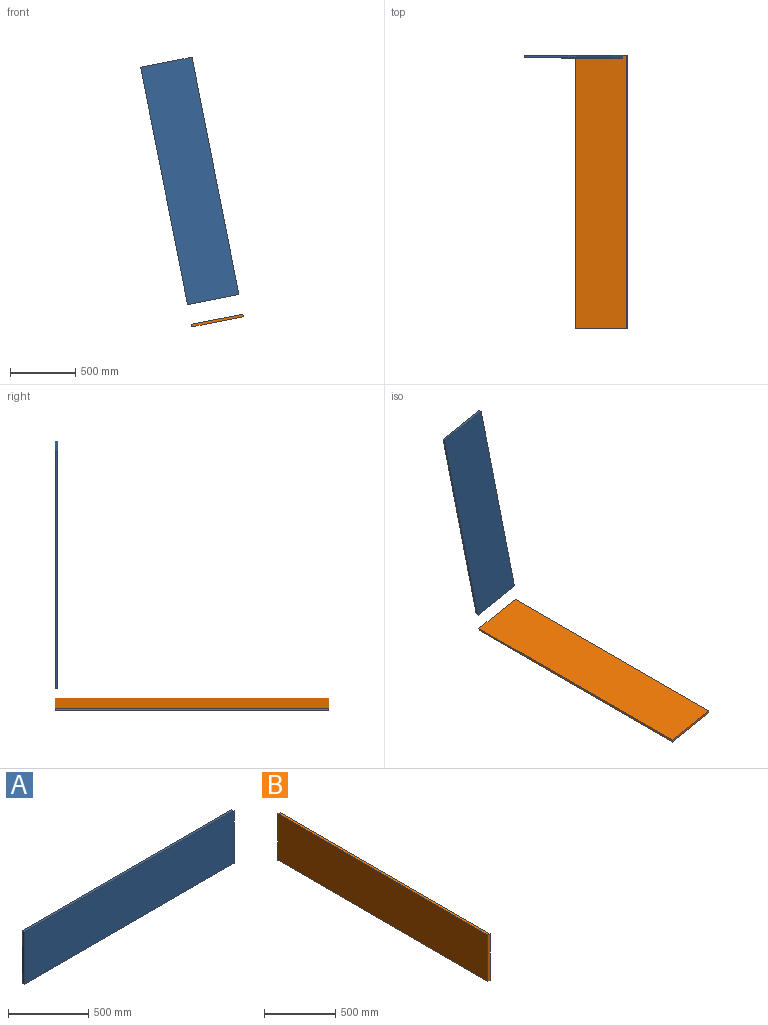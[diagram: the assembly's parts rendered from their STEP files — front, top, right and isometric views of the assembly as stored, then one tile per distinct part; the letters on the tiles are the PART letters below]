
ASSEMBLY  parts=2 mates=2
PART A: 6 faces, bbox 1850x20x400 mm
  f0: plane 400x20mm, normal (1,0,0), area 8000mm2, adj f1,f3,f4,f5
  f1: plane 1850x400mm, normal (0,1,0), area 740000mm2, adj f0,f2,f4,f5
  f2: plane 400x20mm, normal (-1,0,0), area 8000mm2, adj f1,f3,f4,f5
  f3: plane 1850x400mm, normal (0,-1,0), area 740000mm2, adj f0,f2,f4,f5
  f4: plane 1850x20mm, normal (0,0,1), area 37000mm2, adj f0,f1,f2,f3
  f5: plane 1850x20mm, normal (0,0,-1), area 37000mm2, adj f0,f1,f2,f3
PART B: 6 faces, bbox 20x2090x400 mm
  f0: plane 400x20mm, normal (0,1,0), area 8000mm2, adj f1,f3,f4,f5
  f1: plane 2090x400mm, normal (-1,0,0), area 836000mm2, adj f0,f2,f4,f5
  f2: plane 400x20mm, normal (0,-1,0), area 8000mm2, adj f1,f3,f4,f5
  f3: plane 2090x400mm, normal (1,0,0), area 836000mm2, adj f0,f2,f4,f5
  f4: plane 2090x20mm, normal (0,0,1), area 41800mm2, adj f0,f1,f2,f3
  f5: plane 2090x20mm, normal (0,0,-1), area 41800mm2, adj f0,f1,f2,f3
PLACE A rot(axis=(0,1,0),78.8deg) t=(951.52,1032.27,-69.49)mm
PLACE B rot(axis=(0,1,0),78.8deg) t=(1162.21,-2.73,-1137.3)mm
MATE planar A.f1 <-> B.f0  axis (0,1,0) through (1147.74,1042.27,-30.77)mm
MATE planar A.f4 <-> B.f4  axis (0.98,0,0.19) through (1343.95,1032.27,7.94)mm
